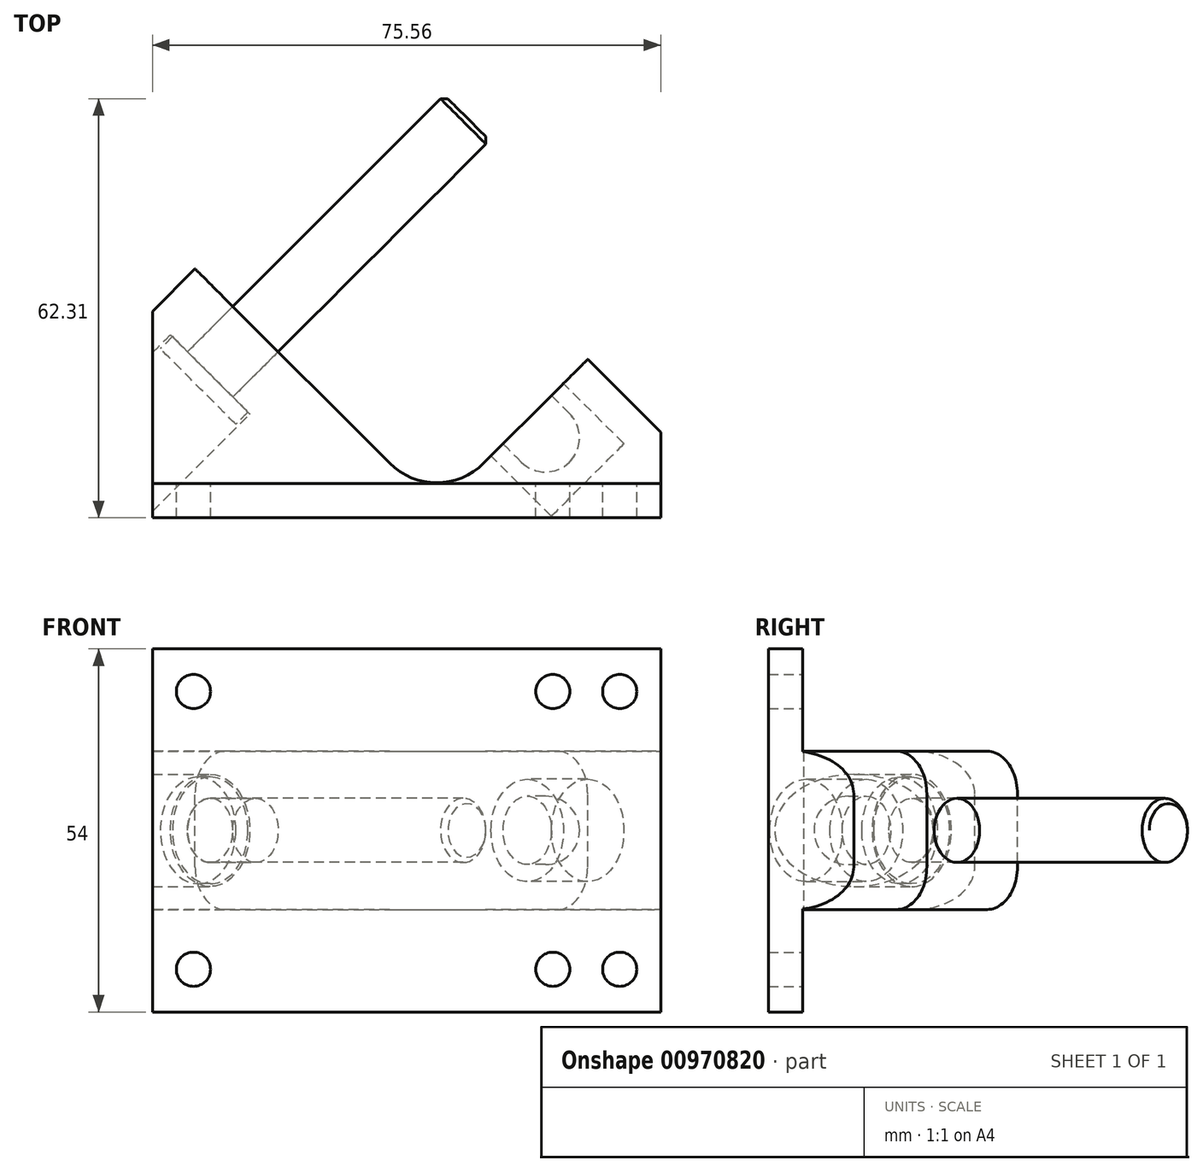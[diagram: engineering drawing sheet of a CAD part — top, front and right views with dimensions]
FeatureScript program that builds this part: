
annotation { "Feature Type Name" : "Feature", "Feature Type Description" : "" }
export const myFeature = defineFeature(function(context is Context, id is Id, definition is map)
    precondition{}
    {
        {
            var Q0;
            Q0=qCreatedBy(makeId("Top.planeOp"),FACE);
            var sketch = newSketch(context, id + "F0", { "sketchPlane" : qUnion([Q0])});
            skLineSegment(sketch, "E0", {"start": v(42.25, 1.1) * mm, "end": v(64.7, 23.56) * mm});
            skLineSegment(sketch, "E1", {"start": v(64.7, 23.56) * mm, "end": v(75.57, 12.7) * mm});
            skLineSegment(sketch, "E2", {"start": v(75.57, 12.7) * mm, "end": v(75.57, 0) * mm});
            skLineSegment(sketch, "E3", {"start": v(75.57, 0) * mm, "end": v(0, 0) * mm});
            skLineSegment(sketch, "E4", {"start": v(0, 0) * mm, "end": v(0, 30.7) * mm});
            skLineSegment(sketch, "E5", {"start": v(0, 30.7) * mm, "end": v(6.33, 37.03) * mm});
            skLineSegment(sketch, "E6", {"start": v(6.33, 37.03) * mm, "end": v(42.25, 1.1) * mm});
            skLineSegment(sketch, "E7", {"start": v(15.31, 28.05) * mm, "end": v(28.78, 41.52) * mm, "construction": true});
            skLineSegment(sketch, "E8", {"start": v(50.34, 9.2) * mm, "end": v(59.32, 0.21) * mm, "construction": true});
            skLineSegment(sketch, "E9", {"start": v(59.32, 0.21) * mm, "end": v(70.1, 10.99) * mm, "construction": true});
            skLineSegment(sketch, "E10", {"start": v(70.1, 10.99) * mm, "end": v(61.11, 19.97) * mm, "construction": true});
            skLineSegment(sketch, "E11", {"start": v(61.11, 19.97) * mm, "end": v(50.34, 9.2) * mm, "construction": true});
            skLineSegment(sketch, "E12", {"start": v(64.7, 5.6) * mm, "end": v(15.31, 55) * mm, "construction": true});
            skPoint(sketch, "E13", {"position": v(58.42, 11.89) * mm});
            skCircle(sketch, "E14", {"center": v(15.31, 55) * mm, "radius": 4 * mm, "construction": true});
            skCircle(sketch, "E15", {"center": v(58.42, 11.89) * mm, "radius": 5.08 * mm, "construction": true});
            skSolve(sketch);
        }
        {
            var Q0;
            Q0=makeQuery(id+"F0.imprint","IMPRINT",FACE,{"disambiguationData":[TD([[makeQuery(id+"F0.imprint","IMPRINT",EDGE,{"derivedFrom":sQuery(id+"F0.wireOp",EDGE,"E14")}),1.0]])]});
            var Q1;
            Q1=makeQuery(id+"F0.imprint","IMPRINT",FACE,{"disambiguationData":[TD([[makeQuery(id+"F0.imprint","IMPRINT",EDGE,{"derivedFrom":sQuery(id+"F0.wireOp",EDGE,"E0")}),-1.0]])]});
            extrude(context, id + "F1", {"entities" : qUnion([Q0, Q1]), "oppositeDirection" : true, "depth" : 27 * mm, "offsetDistance" : 25.4 * mm});
        }
        {
            var Q0;
            Q0=makeQuery(id+"F1.opExtrude","SWEPT_EDGE",EDGE,{"disambiguationData":[OSD([sQuery(id+"F0.wireOp",EDGE,"E0"),sQuery(id+"F0.wireOp",EDGE,"E6")])]});
            fillet(context, id + "F2", {"entities" : qUnion([Q0]), "radius" : 9.9 * mm, "tangentPropagation" : true, "allowEdgeOverflow" : false});
        }
        {
            var Q0;
            Q0=qCreatedBy(makeId("Top.planeOp"),FACE);
            var sketch = newSketch(context, id + "F3", { "sketchPlane" : qUnion([Q0])});
            skLineSegment(sketch, "E16.bottom", {"start": v(0, 5.08) * mm, "end": v(75.57, 5.08) * mm});
            skLineSegment(sketch, "E16.top", {"start": v(0, 37.03) * mm, "end": v(75.57, 37.03) * mm});
            skLineSegment(sketch, "E16.left", {"start": v(0, 5.08) * mm, "end": v(0, 37.03) * mm});
            skLineSegment(sketch, "E16.right", {"start": v(75.57, 5.08) * mm, "end": v(75.57, 37.03) * mm});
            skSolve(sketch);
        }
        {
            var Q0;
            Q0=makeQuery(id+"F3.imprint","IMPRINT",FACE,{"disambiguationData":[TD([[makeQuery(id+"F3.imprint","IMPRINT",EDGE,{"derivedFrom":sQuery(id+"F3.wireOp",EDGE,"E16.bottom")}),1.0]])]});
            extrude(context, id + "F4", {"entities" : qUnion([Q0]), "operationType" : NewBodyOperationType.REMOVE, "oppositeDirection" : true, "depth" : 15.24 * mm, "offsetDistance" : 25.4 * mm});
        }
        {
            var Q0;
            Q0=makeQuery(id+"F4.boolean.opBoolean","COPY",FACE,{"derivedFrom":makeQuery(id+"F4.opExtrude","SWEPT_FACE",FACE,{"disambiguationData":[OSD([sQuery(id+"F3.wireOp",EDGE,"E16.bottom")])]})});
            var sketch = newSketch(context, id + "F5", { "sketchPlane" : qUnion([Q0])});
            skLineSegment(sketch, "E17", {"start": v(-75.57, -6.35) * mm, "end": v(0, -6.35) * mm, "construction": true});
            skCircle(sketch, "E18", {"center": v(-69.47, -6.35) * mm, "radius": 2.54 * mm});
            skCircle(sketch, "E19", {"center": v(-59.53, -6.35) * mm, "radius": 2.54 * mm});
            skCircle(sketch, "E20", {"center": v(-6.1, -6.35) * mm, "radius": 2.54 * mm});
            skSolve(sketch);
        }
        {
            var Q0;
            Q0 = qSketchRegion(id + "F5", true);
            extrude(context, id + "F6", {"entities" : qUnion([Q0]), "operationType" : NewBodyOperationType.REMOVE, "endBound" : BoundingType.THROUGH_ALL, "oppositeDirection" : true, "depth" : 25.4 * mm, "offsetDistance" : 25.4 * mm});
        }
        {
            var Q0;
            Q0=makeQuery(id+"F1.opExtrude","SWEPT_BODY",BODY,{"disambiguationData":[OSD([sQuery(id+"F0.wireOp",EDGE,"E0"),sQuery(id+"F0.wireOp",EDGE,"E1"),sQuery(id+"F0.wireOp",EDGE,"E2"),sQuery(id+"F0.wireOp",EDGE,"E3"),sQuery(id+"F0.wireOp",EDGE,"E4"),sQuery(id+"F0.wireOp",EDGE,"E5"),sQuery(id+"F0.wireOp",EDGE,"E6")])]});
            var Q1;
            Q1=makeQuery(id+"F1.opExtrude","CAP_FACE",FACE,{"disambiguationData":[OSD([sQuery(id+"F0.wireOp",EDGE,"E0"),sQuery(id+"F0.wireOp",EDGE,"E1"),sQuery(id+"F0.wireOp",EDGE,"E2"),sQuery(id+"F0.wireOp",EDGE,"E3"),sQuery(id+"F0.wireOp",EDGE,"E4"),sQuery(id+"F0.wireOp",EDGE,"E5"),sQuery(id+"F0.wireOp",EDGE,"E6")])],"isStart":false});
            mirror(context, id + "F7", {"operationType" : NewBodyOperationType.ADD, "entities" : qUnion([Q0]), "mirrorPlane" : qUnion([Q1])});
        }
        {
            var Q0;
            Q0=makeQuery(id+"F7.opPattern","COPY",EDGE,{"derivedFrom":makeQuery(id+"F4.boolean.opBoolean","INTERSECT",EDGE,{"derivedFrom":[makeQuery(id+"F1.opExtrude","SWEPT_FACE",FACE,{"disambiguationData":[OSD([sQuery(id+"F0.wireOp",EDGE,"E1")])]}),makeQuery(id+"F4.opExtrude","CAP_FACE",FACE,{"disambiguationData":[OSD([sQuery(id+"F3.wireOp",EDGE,"E16.bottom"),sQuery(id+"F3.wireOp",EDGE,"E16.top"),sQuery(id+"F3.wireOp",EDGE,"E16.left"),sQuery(id+"F3.wireOp",EDGE,"E16.right")])],"isStart":false})]}),"instanceName":"1"});
            var Q1;
            Q1=makeQuery(id+"F4.boolean.opBoolean","INTERSECT",EDGE,{"derivedFrom":[makeQuery(id+"F1.opExtrude","SWEPT_FACE",FACE,{"disambiguationData":[OSD([sQuery(id+"F0.wireOp",EDGE,"E1")])]}),makeQuery(id+"F4.opExtrude","CAP_FACE",FACE,{"disambiguationData":[OSD([sQuery(id+"F3.wireOp",EDGE,"E16.bottom"),sQuery(id+"F3.wireOp",EDGE,"E16.top"),sQuery(id+"F3.wireOp",EDGE,"E16.left"),sQuery(id+"F3.wireOp",EDGE,"E16.right")])],"isStart":false})]});
            var Q2;
            Q2=makeQuery(id+"F7.opPattern","COPY",EDGE,{"derivedFrom":makeQuery(id+"F4.boolean.opBoolean","INTERSECT",EDGE,{"derivedFrom":[makeQuery(id+"F1.opExtrude","SWEPT_FACE",FACE,{"disambiguationData":[OSD([sQuery(id+"F0.wireOp",EDGE,"E5")])]}),makeQuery(id+"F4.opExtrude","CAP_FACE",FACE,{"disambiguationData":[OSD([sQuery(id+"F3.wireOp",EDGE,"E16.bottom"),sQuery(id+"F3.wireOp",EDGE,"E16.top"),sQuery(id+"F3.wireOp",EDGE,"E16.left"),sQuery(id+"F3.wireOp",EDGE,"E16.right")])],"isStart":false})]}),"instanceName":"1"});
            var Q3;
            Q3=makeQuery(id+"F4.boolean.opBoolean","INTERSECT",EDGE,{"derivedFrom":[makeQuery(id+"F1.opExtrude","SWEPT_FACE",FACE,{"disambiguationData":[OSD([sQuery(id+"F0.wireOp",EDGE,"E5")])]}),makeQuery(id+"F4.opExtrude","CAP_FACE",FACE,{"disambiguationData":[OSD([sQuery(id+"F3.wireOp",EDGE,"E16.bottom"),sQuery(id+"F3.wireOp",EDGE,"E16.top"),sQuery(id+"F3.wireOp",EDGE,"E16.left"),sQuery(id+"F3.wireOp",EDGE,"E16.right")])],"isStart":false})]});
            fillet(context, id + "F8", {"entities" : qUnion([Q0, Q1, Q2, Q3]), "radius" : 6.35 * mm, "tangentPropagation" : true, "allowEdgeOverflow" : false});
        }
        {
            var Q0;
            Q0=qCreatedBy(makeId("Top.planeOp"),FACE);
            var sketch = newSketch(context, id + "F9", { "sketchPlane" : qUnion([Q0])});
            skLineSegment(sketch, "E21", {"start": v(15.31, 28.05) * mm, "end": v(-6.37, 6.37) * mm});
            skLineSegment(sketch, "E22", {"start": v(-6.37, 6.37) * mm, "end": v(-12.27, 12.27) * mm});
            skLineSegment(sketch, "E23", {"start": v(-12.27, 12.27) * mm, "end": v(2.68, 27.22) * mm});
            skLineSegment(sketch, "E24", {"start": v(2.68, 27.22) * mm, "end": v(5.21, 24.68) * mm});
            skLineSegment(sketch, "E25", {"start": v(5.21, 24.68) * mm, "end": v(11.95, 31.42) * mm});
            skLineSegment(sketch, "E26", {"start": v(11.95, 31.42) * mm, "end": v(15.31, 28.05) * mm});
            skLineSegment(sketch, "E27", {"start": v(0, 0) * mm, "end": v(-12.27, 12.27) * mm, "construction": true});
            skSolve(sketch);
        }
        {
            var Q0;
            Q0=makeQuery(id+"F1.opExtrude","SWEPT_BODY",BODY,{"disambiguationData":[OSD([sQuery(id+"F0.wireOp",EDGE,"E0"),sQuery(id+"F0.wireOp",EDGE,"E1"),sQuery(id+"F0.wireOp",EDGE,"E2"),sQuery(id+"F0.wireOp",EDGE,"E3"),sQuery(id+"F0.wireOp",EDGE,"E4"),sQuery(id+"F0.wireOp",EDGE,"E5"),sQuery(id+"F0.wireOp",EDGE,"E6")])]});
            transform(context, id + "F10", {"entities" : qUnion([Q0]), "transformType" : TransformType.TRANSLATION_3D, "dx" : 0 * mm, "dy" : 0 * mm, "dz" : 27 * mm, "makeCopy" : false});
        }
        {
            var Q0;
            Q0 = qSketchRegion(id + "F9", true);
            var Q1;
            Q1=sQuery(id+"F0.wireOp",EDGE,"E7");
            revolve(context, id + "F11", {"operationType" : NewBodyOperationType.REMOVE, "surfaceOperationType" : NewSurfaceOperationType.NEW, "entities" : qUnion([Q0]), "axis" : qUnion([Q1]), "revolveType" : RevolveType.FULL, "oppositeDirection" : true});
        }
        {
            var Q0;
            Q0=qCreatedBy(makeId("Top.planeOp"),FACE);
            var sketch = newSketch(context, id + "F12", { "sketchPlane" : qUnion([Q0])});
            skLineSegment(sketch, "E28.1", {"start": v(2.97, 26.93) * mm, "end": v(5.21, 24.68) * mm});
            skLineSegment(sketch, "E28.2", {"start": v(5.21, 24.68) * mm, "end": v(11.95, 31.42) * mm});
            skLineSegment(sketch, "E29", {"start": v(2.97, 26.93) * mm, "end": v(1.17, 25.13) * mm});
            skPoint(sketch, "E28.0.start.orphan", {"position": v(-12.27, 12.27) * mm});
            skLineSegment(sketch, "E30", {"start": v(1.17, 25.13) * mm, "end": v(6.78, 19.52) * mm});
            skLineSegment(sketch, "E31", {"start": v(6.78, 19.52) * mm, "end": v(46.74, 59.48) * mm});
            skLineSegment(sketch, "E32", {"start": v(46.74, 59.48) * mm, "end": v(43.38, 62.85) * mm});
            skLineSegment(sketch, "E33", {"start": v(43.38, 62.85) * mm, "end": v(11.95, 31.42) * mm});
            skSolve(sketch);
        }
        {
            var Q0;
            Q0=makeQuery(id+"F12.imprint","IMPRINT",FACE,{"disambiguationData":[TD([[makeQuery(id+"F12.imprint","IMPRINT",EDGE,{"derivedFrom":sQuery(id+"F12.wireOp",EDGE,"E28.1")}),-1.0]])]});
            var Q1;
            Q1=sQuery(id+"F12.wireOp",EDGE,"E31");
            revolve(context, id + "F13", {"surfaceOperationType" : NewSurfaceOperationType.NEW, "entities" : qUnion([Q0]), "axis" : qUnion([Q1]), "revolveType" : RevolveType.FULL});
        }
        {
            var Q0;
            Q0=makeQuery(id+"F13.opRevolve","SWEPT_EDGE",EDGE,{"disambiguationData":[OSD([sQuery(id+"F12.wireOp",EDGE,"E32"),sQuery(id+"F12.wireOp",EDGE,"E33")])]});
            chamfer(context, id + "F14", {"entities" : qUnion([Q0]), "width" : 0.76 * mm, "tangentPropagation" : true});
        }
        {
            var Q0;
            Q0=qCreatedBy(makeId("Top.planeOp"),FACE);
            var sketch = newSketch(context, id + "F15", { "sketchPlane" : qUnion([Q0])});
            skLineSegment(sketch, "E34.0", {"start": v(70.1, 10.99) * mm, "end": v(61.11, 19.97) * mm});
            skLineSegment(sketch, "E34.1", {"start": v(64.7, 5.6) * mm, "end": v(70.1, 10.99) * mm});
            skLineSegment(sketch, "E34.4", {"start": v(64.7, 5.6) * mm, "end": v(55.72, 14.58) * mm});
            skPoint(sketch, "E34.5", {"position": v(58.42, 11.89) * mm});
            skPoint(sketch, "E35.orphan", {"position": v(59.32, 0.21) * mm});
            skLineSegment(sketch, "E36", {"start": v(61.11, 19.97) * mm, "end": v(55.72, 14.58) * mm});
            skPoint(sketch, "E37.orphan", {"position": v(15.31, 55) * mm});
            skSolve(sketch);
        }
        {
            var Q0;
            Q0 = qSketchRegion(id + "F15", true);
            var Q1;
            Q1=sQuery(id+"F15.wireOp",EDGE,"E34.4");
            revolve(context, id + "F16", {"operationType" : NewBodyOperationType.REMOVE, "surfaceOperationType" : NewSurfaceOperationType.NEW, "entities" : qUnion([Q0]), "axis" : qUnion([Q1]), "revolveType" : RevolveType.FULL, "oppositeDirection" : true});
        }
        {
            var Q0;
            Q0=qCreatedBy(makeId("Top.planeOp"),FACE);
            var sketch = newSketch(context, id + "F17", { "sketchPlane" : qUnion([Q0])});
            skLineSegment(sketch, "E38", {"start": v(60.21, 19.07) * mm, "end": v(61.11, 19.97) * mm});
            skArc(sketch, "E39.0", {"start": v(62.01, 8.3) * mm, "mid": v(63.5, 11.89) * mm, "end": v(62.01, 15.48) * mm});
            skLineSegment(sketch, "E40", {"start": v(59.32, 18.17) * mm, "end": v(62.01, 15.48) * mm});
            skLineSegment(sketch, "E41.0", {"start": v(64.7, 5.6) * mm, "end": v(62.01, 8.3) * mm});
            skLineSegment(sketch, "E42.0", {"start": v(70.1, 10.99) * mm, "end": v(61.11, 19.97) * mm});
            skLineSegment(sketch, "E43.trimOffspring", {"start": v(64.7, 5.6) * mm, "end": v(70.1, 10.99) * mm});
            skPoint(sketch, "E44.trimOffspring.end.orphan", {"position": v(15.31, 55) * mm});
            skLineSegment(sketch, "E45", {"start": v(59.32, 18.17) * mm, "end": v(61.11, 19.97) * mm});
            skSolve(sketch);
        }
        {
            var Q0;
            Q0=qCreatedBy(makeId("Top.planeOp"),FACE);
            var sketch = newSketch(context, id + "F18", { "sketchPlane" : qUnion([Q0])});
            skLineSegment(sketch, "E46.0", {"start": v(64.7, 5.6) * mm, "end": v(70.1, 10.99) * mm});
            skLineSegment(sketch, "E46.1", {"start": v(70.1, 10.99) * mm, "end": v(61.11, 19.97) * mm});
            skArc(sketch, "E46.2", {"start": v(62.01, 8.3) * mm, "mid": v(63.5, 11.89) * mm, "end": v(62.01, 15.48) * mm});
            skLineSegment(sketch, "E46.3", {"start": v(59.32, 18.17) * mm, "end": v(62.01, 15.48) * mm});
            skLineSegment(sketch, "E46.5", {"start": v(60.21, 19.07) * mm, "end": v(61.11, 19.97) * mm});
            skLineSegment(sketch, "E46.6", {"start": v(64.7, 5.6) * mm, "end": v(62.01, 8.3) * mm});
            skLineSegment(sketch, "E47", {"start": v(59.32, 18.17) * mm, "end": v(60.21, 19.07) * mm});
            skSolve(sketch);
        }
        {
            var Q0;
            Q0 = qSketchRegion(id + "F18", true);
            var Q1;
            Q1=sQuery(id+"F0.wireOp",EDGE,"E12");
            revolve(context, id + "F19", {"surfaceOperationType" : NewSurfaceOperationType.NEW, "entities" : qUnion([Q0]), "axis" : qUnion([Q1]), "revolveType" : RevolveType.FULL, "oppositeDirection" : true});
        }
    });
